# Revit family: Towel Bar-Brizo-Traditional_Series-Bath-Towel Bar-69518_69524
name_source: partatom
category: Specialty Equipment
units: mm (PartAtom-declared; Revit-internal decimal feet)

## family parameters
Always vertical = Yes
Cut with Voids When Loaded = No
OmniClass Number = 23.45.00.00
OmniClass Title = Sanitary, Laundry, and Cleaning Equipment
Part Type = Normal
Room Calculation Point = No
Round Connector Dimension = Use Diameter
Shared = No
Work Plane-Based = Yes

## types (1)
- 18" Towel Bar - Brillance Brushed Bronze
    Assembly Code = C1030200
    Default Elevation = 4' - 0"
    Description = Towel Bar
    Finish = Bronze-Brizo-Venetian Bronze
    Manufacturer = Brizo
    Model = 69518-BZ
    Product Documentation Link = https://media.brizo.com
    Product Name = Traditional Series
    Style = Towel Bar
    Type Comments = Brillance Brushed Bronze
    URL = http://www.brizo.com
    Width = 1' - 6"

## geometry (parser evidence)
native form markers: Blend x2, Sweep x2
no freeform markers — native parametric forms only
